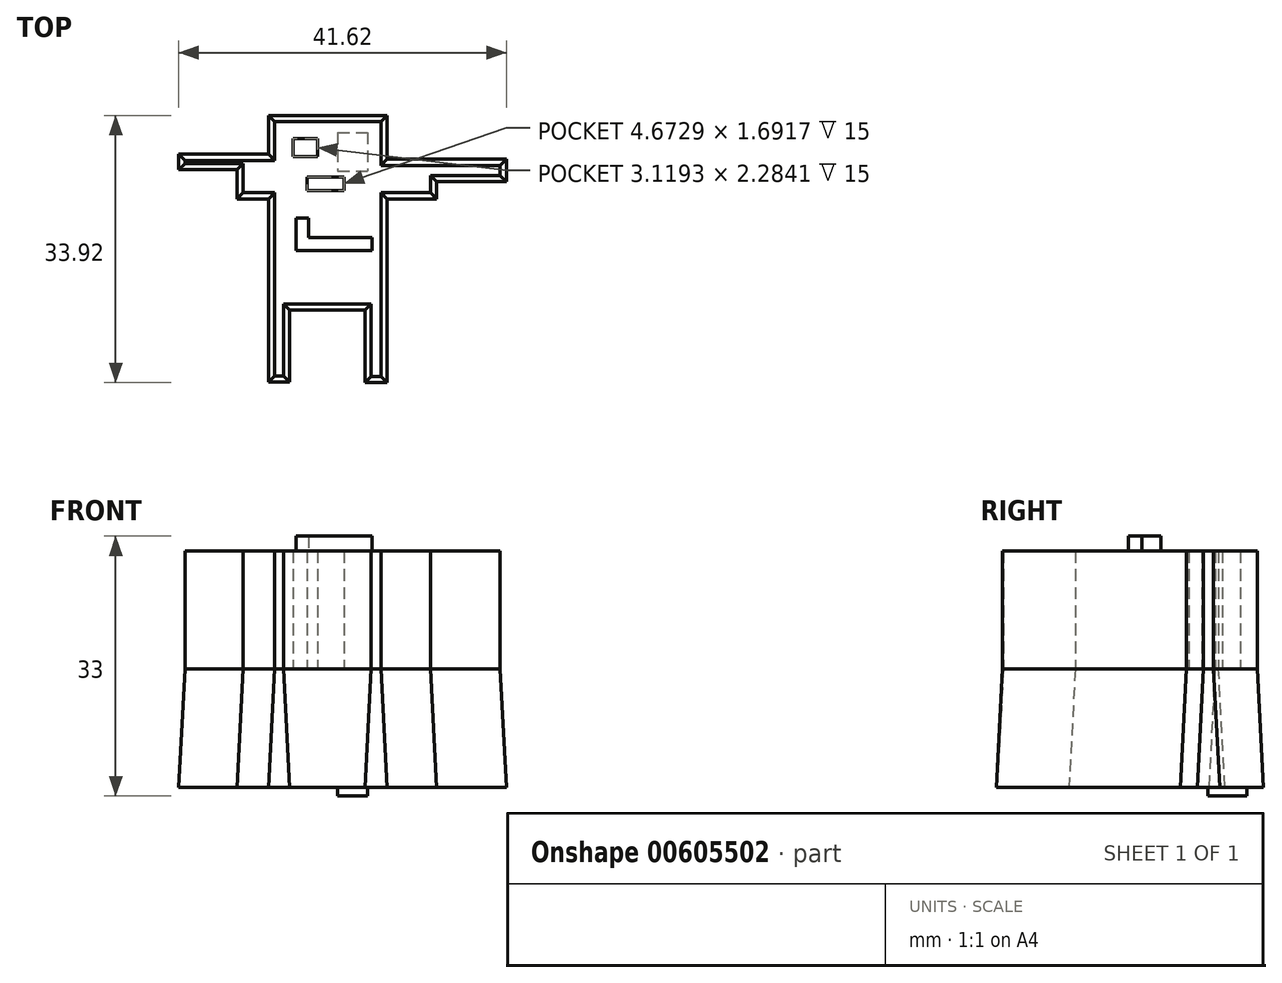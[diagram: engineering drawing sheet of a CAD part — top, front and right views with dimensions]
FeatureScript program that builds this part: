
annotation { "Feature Type Name" : "Feature", "Feature Type Description" : "" }
export const myFeature = defineFeature(function(context is Context, id is Id, definition is map)
    precondition{}
    {
        {
            var Q0;
            Q0=qCreatedBy(makeId("Top.planeOp"),FACE);
            var sketch = newSketch(context, id + "F0", { "sketchPlane" : qUnion([Q0])});
            skLineSegment(sketch, "E0.bottom", {"start": v(-0.5, 23.35) * mm, "end": v(14.55, 23.35) * mm});
            skLineSegment(sketch, "E0.top", {"start": v(-0.5, 9.23) * mm, "end": v(14.55, 9.23) * mm});
            skLineSegment(sketch, "E0.left", {"start": v(-0.5, 23.35) * mm, "end": v(-0.5, 9.23) * mm});
            skLineSegment(sketch, "E0.right", {"start": v(14.55, 23.35) * mm, "end": v(14.55, 9.23) * mm});
            skLineSegment(sketch, "E1.bottom", {"start": v(-0.5, 23.35) * mm, "end": v(-4.53, 23.35) * mm});
            skLineSegment(sketch, "E1.top", {"start": v(-0.5, 29.02) * mm, "end": v(-4.53, 29.02) * mm});
            skLineSegment(sketch, "E1.left", {"start": v(-0.5, 23.35) * mm, "end": v(-0.5, 29.02) * mm});
            skLineSegment(sketch, "E1.right", {"start": v(-4.53, 23.35) * mm, "end": v(-4.53, 29.02) * mm});
            skLineSegment(sketch, "E2.bottom", {"start": v(14.55, 23.35) * mm, "end": v(20.83, 23.35) * mm});
            skLineSegment(sketch, "E2.top", {"start": v(14.55, 28.37) * mm, "end": v(20.83, 28.37) * mm});
            skLineSegment(sketch, "E2.left", {"start": v(14.55, 23.35) * mm, "end": v(14.55, 28.37) * mm});
            skLineSegment(sketch, "E2.right", {"start": v(20.83, 23.35) * mm, "end": v(20.83, 28.37) * mm});
            skLineSegment(sketch, "E3.bottom", {"start": v(14.55, 28.37) * mm, "end": v(-0.5, 28.37) * mm});
            skLineSegment(sketch, "E3.top", {"start": v(14.55, 33.92) * mm, "end": v(-0.5, 33.92) * mm});
            skLineSegment(sketch, "E3.left", {"start": v(14.55, 28.37) * mm, "end": v(14.55, 33.92) * mm});
            skLineSegment(sketch, "E3.right", {"start": v(-0.5, 28.37) * mm, "end": v(-0.5, 33.92) * mm});
            skLineSegment(sketch, "E4.bottom", {"start": v(20.83, 28.37) * mm, "end": v(29.71, 28.37) * mm});
            skLineSegment(sketch, "E4.top", {"start": v(20.83, 25.53) * mm, "end": v(29.71, 25.53) * mm});
            skLineSegment(sketch, "E4.left", {"start": v(20.83, 28.37) * mm, "end": v(20.83, 25.53) * mm});
            skLineSegment(sketch, "E4.right", {"start": v(29.71, 28.37) * mm, "end": v(29.71, 25.53) * mm});
            skLineSegment(sketch, "E5.bottom", {"start": v(-4.53, 29.02) * mm, "end": v(-11.91, 29.02) * mm});
            skLineSegment(sketch, "E5.top", {"start": v(-4.53, 27.04) * mm, "end": v(-11.91, 27.04) * mm});
            skLineSegment(sketch, "E5.left", {"start": v(-4.53, 29.02) * mm, "end": v(-4.53, 27.04) * mm});
            skLineSegment(sketch, "E5.right", {"start": v(-11.91, 29.02) * mm, "end": v(-11.91, 27.04) * mm});
            skLineSegment(sketch, "E6.bottom", {"start": v(-0.5, 9.23) * mm, "end": v(2.2, 9.23) * mm});
            skLineSegment(sketch, "E6.top", {"start": v(-0.5, 0.08) * mm, "end": v(2.2, 0.08) * mm});
            skLineSegment(sketch, "E6.left", {"start": v(-0.5, 9.23) * mm, "end": v(-0.5, 0.08) * mm});
            skLineSegment(sketch, "E6.right", {"start": v(2.2, 9.23) * mm, "end": v(2.2, 0.08) * mm});
            skLineSegment(sketch, "E7.bottom", {"start": v(1.66, 30.36) * mm, "end": v(7.02, 30.36) * mm});
            skLineSegment(sketch, "E7.top", {"start": v(1.66, 28.37) * mm, "end": v(7.02, 28.37) * mm});
            skLineSegment(sketch, "E7.left", {"start": v(1.66, 30.36) * mm, "end": v(1.66, 28.37) * mm});
            skLineSegment(sketch, "E7.right", {"start": v(7.02, 30.36) * mm, "end": v(7.02, 28.37) * mm});
            skLineSegment(sketch, "E8.bottom", {"start": v(27.02, 39.57) * mm, "end": v(-12.98, 39.57) * mm, "construction": true});
            skLineSegment(sketch, "E8.top", {"start": v(27.02, -0.43) * mm, "end": v(-12.98, -0.43) * mm, "construction": true});
            skLineSegment(sketch, "E8.left", {"start": v(27.02, 39.57) * mm, "end": v(27.02, -0.43) * mm, "construction": true});
            skLineSegment(sketch, "E8.right", {"start": v(-12.98, 39.57) * mm, "end": v(-12.98, -0.43) * mm, "construction": true});
            skPoint(sketch, "E8.middle", {"position": v(7.02, 19.57) * mm});
            skPoint(sketch, "E8.middle.positionSnap0", {"position": v(7.02, 29.36) * mm});
            skPoint(sketch, "E8.centerSnap0", {"position": v(7.02, 29.36) * mm});
            skLineSegment(sketch, "E9.bottom", {"start": v(14.55, 9.23) * mm, "end": v(11.73, 9.23) * mm});
            skLineSegment(sketch, "E9.top", {"start": v(14.55, 0) * mm, "end": v(11.73, 0) * mm});
            skLineSegment(sketch, "E9.left", {"start": v(14.55, 9.23) * mm, "end": v(14.55, 0) * mm});
            skLineSegment(sketch, "E9.right", {"start": v(11.73, 9.23) * mm, "end": v(11.73, 0) * mm});
            skSolve(sketch);
        }
        {
            var Q0;
            Q0=makeQuery(id+"F0.imprint","IMPRINT",FACE,{"disambiguationData":[TD([[makeQuery(id+"F0.imprint","IMPRINT",EDGE,{"derivedFrom":sQuery(id+"F0.wireOp",EDGE,"E0.bottom")}),-1.0]])]});
            var Q1;
            {var subQ3=sQuery(id+"F0.wireOp",EDGE,"E2.bottom");Q1=makeQuery(id+"F0.imprint","IMPRINT",FACE,{"disambiguationData":[TD([[makeQuery(id+"F0.imprint","IMPRINT",EDGE,{"derivedFrom":subQ3}),1.0]])]});}
            var Q2;
            {var subQ4=sQuery(id+"F0.wireOp",EDGE,"E0.bottom");Q2=makeQuery(id+"F0.imprint","IMPRINT",FACE,{"disambiguationData":[TD([[makeQuery(id+"F0.imprint","IMPRINT",EDGE,{"derivedFrom":subQ4}),1.0]])]});}
            var Q3;
            {var subQ0=sQuery(id+"F0.wireOp",EDGE,"E5.bottom");Q3=makeQuery(id+"F0.imprint","IMPRINT",FACE,{"disambiguationData":[TD([[makeQuery(id+"F0.imprint","IMPRINT",EDGE,{"derivedFrom":subQ0}),1.0]])]});}
            var Q4;
            {var subQ3=sQuery(id+"F0.wireOp",EDGE,"E1.bottom");Q4=makeQuery(id+"F0.imprint","IMPRINT",FACE,{"disambiguationData":[TD([[makeQuery(id+"F0.imprint","IMPRINT",EDGE,{"derivedFrom":subQ3}),-1.0]])]});}
            var Q5;
            Q5=makeQuery(id+"F0.imprint","IMPRINT",FACE,{"disambiguationData":[TD([[makeQuery(id+"F0.imprint","IMPRINT",EDGE,{"derivedFrom":sQuery(id+"F0.wireOp",EDGE,"E7.bottom")}),-1.0]])]});
            var Q6;
            Q6=makeQuery(id+"F0.imprint","IMPRINT",FACE,{"disambiguationData":[TD([[makeQuery(id+"F0.imprint","IMPRINT",EDGE,{"derivedFrom":sQuery(id+"F0.wireOp",EDGE,"E3.top")}),1.0]])]});
            var Q7;
            Q7=makeQuery(id+"F0.imprint","IMPRINT",FACE,{"disambiguationData":[TD([[makeQuery(id+"F0.imprint","IMPRINT",EDGE,{"derivedFrom":sQuery(id+"F0.wireOp",EDGE,"r1xIN93y-4Mna-sWwQ-LPJp-I6mFRcgzbT0e.bottom")}),1.0]])]});
            var Q8;
            Q8=makeQuery(id+"F0.imprint","IMPRINT",FACE,{"disambiguationData":[TD([[makeQuery(id+"F0.imprint","IMPRINT",EDGE,{"derivedFrom":sQuery(id+"F0.wireOp",EDGE,"E6.top")}),1.0]])]});
            var Q9;
            {var subQ0=sQuery(id+"F0.wireOp",EDGE,"E4.bottom");Q9=makeQuery(id+"F0.imprint","IMPRINT",FACE,{"disambiguationData":[TD([[makeQuery(id+"F0.imprint","IMPRINT",EDGE,{"derivedFrom":subQ0}),-1.0]])]});}
            var Q10;
            Q10=makeQuery(id+"F0.imprint","IMPRINT",FACE,{"disambiguationData":[TD([[makeQuery(id+"F0.imprint","IMPRINT",EDGE,{"derivedFrom":sQuery(id+"F0.wireOp",EDGE,"E9.top")}),-1.0]])]});
            extrude(context, id + "F1", {"entities" : qUnion([Q0, Q1, Q2, Q3, Q4, Q5, Q6, Q7, Q8, Q9, Q10]), "depth" : 15 * mm, "offsetDistance" : 25 * mm, "hasDraft" : true, "draftAngle" : 3 * degree, "draftPullDirection" : true});
        }
        {
            var Q0;
            Q0=makeQuery(id+"F1.opExtrude","CAP_FACE",FACE,{"disambiguationData":[OSD([sQuery(id+"F0.wireOp",EDGE,"E0.top"),sQuery(id+"F0.wireOp",EDGE,"E0.left"),sQuery(id+"F0.wireOp",EDGE,"E0.right"),sQuery(id+"F0.wireOp",EDGE,"E1.bottom"),sQuery(id+"F0.wireOp",EDGE,"E1.top"),sQuery(id+"F0.wireOp",EDGE,"E1.right"),sQuery(id+"F0.wireOp",EDGE,"E2.bottom"),sQuery(id+"F0.wireOp",EDGE,"E2.top"),sQuery(id+"F0.wireOp",EDGE,"E2.right"),sQuery(id+"F0.wireOp",EDGE,"E3.top"),sQuery(id+"F0.wireOp",EDGE,"E3.left"),sQuery(id+"F0.wireOp",EDGE,"E3.right"),sQuery(id+"F0.wireOp",EDGE,"E4.bottom"),sQuery(id+"F0.wireOp",EDGE,"E4.top"),sQuery(id+"F0.wireOp",EDGE,"E4.right"),sQuery(id+"F0.wireOp",EDGE,"E5.bottom"),sQuery(id+"F0.wireOp",EDGE,"E5.top"),sQuery(id+"F0.wireOp",EDGE,"E5.right"),sQuery(id+"F0.wireOp",EDGE,"E6.top"),sQuery(id+"F0.wireOp",EDGE,"E6.left"),sQuery(id+"F0.wireOp",EDGE,"E6.right"),sQuery(id+"F0.wireOp",EDGE,"E9.top"),sQuery(id+"F0.wireOp",EDGE,"E9.left"),sQuery(id+"F0.wireOp",EDGE,"E9.right")])],"isStart":false});
            var sketch = newSketch(context, id + "F2", { "sketchPlane" : qUnion([Q0])});
            skLineSegment(sketch, "E10.bottom", {"start": v(2.6, 31) * mm, "end": v(5.71, 31) * mm});
            skLineSegment(sketch, "E10.top", {"start": v(2.6, 28.72) * mm, "end": v(5.71, 28.72) * mm});
            skLineSegment(sketch, "E10.left", {"start": v(2.6, 31) * mm, "end": v(2.6, 28.72) * mm});
            skLineSegment(sketch, "E10.right", {"start": v(5.71, 31) * mm, "end": v(5.71, 28.72) * mm});
            skLineSegment(sketch, "E11.bottom", {"start": v(4.4, 26.11) * mm, "end": v(9.08, 26.11) * mm});
            skLineSegment(sketch, "E11.top", {"start": v(4.4, 24.42) * mm, "end": v(9.08, 24.42) * mm});
            skLineSegment(sketch, "E11.left", {"start": v(4.4, 26.11) * mm, "end": v(4.4, 24.42) * mm});
            skLineSegment(sketch, "E11.right", {"start": v(9.08, 26.11) * mm, "end": v(9.08, 24.42) * mm});
            skSolve(sketch);
        }
        {
            var Q0;
            Q0=makeQuery(id+"F2.imprint","IMPRINT",FACE,{"disambiguationData":[TD([[makeQuery(id+"F2.imprint","IMPRINT",EDGE,{"derivedFrom":sQuery(id+"F2.wireOp",EDGE,"E10.bottom")}),1.0]])]});
            var sketch = newSketch(context, id + "F3", { "sketchPlane" : qUnion([Q0])});
            skLineSegment(sketch, "E12.bottom", {"start": v(8.23, 31.04) * mm, "end": v(11.91, 31.04) * mm});
            skLineSegment(sketch, "E12.top", {"start": v(8.23, 27.89) * mm, "end": v(11.91, 27.89) * mm});
            skLineSegment(sketch, "E12.left", {"start": v(8.23, 31.04) * mm, "end": v(8.23, 27.89) * mm});
            skLineSegment(sketch, "E12.right", {"start": v(11.91, 31.04) * mm, "end": v(11.91, 27.89) * mm});
            skSolve(sketch);
        }
        {
            var Q0;
            Q0=makeQuery(id+"F2.imprint","IMPRINT",FACE,{"disambiguationData":[TD([[makeQuery(id+"F2.imprint","IMPRINT",EDGE,{"derivedFrom":sQuery(id+"F2.wireOp",EDGE,"E10.bottom")}),1.0]])]});
            var Q1;
            Q1=makeQuery(id+"F3.imprint","IMPRINT",FACE,{"disambiguationData":[TD([[makeQuery(id+"F3.imprint","IMPRINT",EDGE,{"derivedFrom":sQuery(id+"F3.wireOp",EDGE,"E12.bottom")}),-1.0]])]});
            extrude(context, id + "F4", {"entities" : qUnion([Q0, Q1]), "operationType" : NewBodyOperationType.ADD, "depth" : 15 * mm, "offsetDistance" : 25 * mm});
        }
        {
            var Q0;
            Q0=makeQuery(id+"F4.opExtrude","CAP_FACE",FACE,{"disambiguationData":[OSD([sQuery(id+"F0.wireOp",EDGE,"E0.top"),sQuery(id+"F0.wireOp",EDGE,"E0.left"),sQuery(id+"F0.wireOp",EDGE,"E0.right"),sQuery(id+"F0.wireOp",EDGE,"E1.bottom"),sQuery(id+"F0.wireOp",EDGE,"E1.top"),sQuery(id+"F0.wireOp",EDGE,"E1.right"),sQuery(id+"F0.wireOp",EDGE,"E2.bottom"),sQuery(id+"F0.wireOp",EDGE,"E2.top"),sQuery(id+"F0.wireOp",EDGE,"E2.right"),sQuery(id+"F0.wireOp",EDGE,"E3.top"),sQuery(id+"F0.wireOp",EDGE,"E3.left"),sQuery(id+"F0.wireOp",EDGE,"E3.right"),sQuery(id+"F0.wireOp",EDGE,"E4.bottom"),sQuery(id+"F0.wireOp",EDGE,"E4.top"),sQuery(id+"F0.wireOp",EDGE,"E4.right"),sQuery(id+"F0.wireOp",EDGE,"E5.bottom"),sQuery(id+"F0.wireOp",EDGE,"E5.top"),sQuery(id+"F0.wireOp",EDGE,"E5.right"),sQuery(id+"F0.wireOp",EDGE,"E6.top"),sQuery(id+"F0.wireOp",EDGE,"E6.left"),sQuery(id+"F0.wireOp",EDGE,"E6.right"),sQuery(id+"F0.wireOp",EDGE,"E9.top"),sQuery(id+"F0.wireOp",EDGE,"E9.left"),sQuery(id+"F0.wireOp",EDGE,"E9.right"),sQuery(id+"F2.wireOp",EDGE,"E10.bottom"),sQuery(id+"F2.wireOp",EDGE,"E10.top"),sQuery(id+"F2.wireOp",EDGE,"E10.left"),sQuery(id+"F2.wireOp",EDGE,"E10.right"),sQuery(id+"F2.wireOp",EDGE,"E11.bottom"),sQuery(id+"F2.wireOp",EDGE,"E11.top"),sQuery(id+"F2.wireOp",EDGE,"E11.left"),sQuery(id+"F2.wireOp",EDGE,"E11.right")])],"isStart":false});
            var sketch = newSketch(context, id + "F5", { "sketchPlane" : qUnion([Q0])});
            skLineSegment(sketch, "E13.bottom", {"start": v(8.28, 31.8) * mm, "end": v(12.06, 31.8) * mm});
            skLineSegment(sketch, "E13.top", {"start": v(8.28, 26.87) * mm, "end": v(12.06, 26.87) * mm});
            skLineSegment(sketch, "E13.left", {"start": v(8.28, 31.8) * mm, "end": v(8.28, 26.87) * mm});
            skLineSegment(sketch, "E13.right", {"start": v(12.06, 31.8) * mm, "end": v(12.06, 26.87) * mm});
            skPoint(sketch, "E14.oppositeSnap0", {"position": v(8.28, 29.33) * mm});
            skLineSegment(sketch, "E14.bottom", {"start": v(8.28, 29.33) * mm, "end": v(6.8, 29.33) * mm});
            skLineSegment(sketch, "E14.top", {"start": v(8.28, 29.33) * mm, "end": v(6.8, 29.33) * mm});
            skLineSegment(sketch, "E14.left", {"start": v(8.28, 29.33) * mm, "end": v(8.28, 29.33) * mm});
            skLineSegment(sketch, "E14.right", {"start": v(6.8, 29.33) * mm, "end": v(6.8, 29.33) * mm});
            skSolve(sketch);
        }
        {
            var Q0;
            {var subQ3=sQuery(id+"F5.wireOp",EDGE,"E13.bottom");Q0=makeQuery(id+"F5.imprint","IMPRINT",FACE,{"disambiguationData":[TD([[makeQuery(id+"F5.imprint","IMPRINT",EDGE,{"derivedFrom":subQ3}),-1.0]])]});}
            extrude(context, id + "F6", {"entities" : qUnion([Q0]), "operationType" : NewBodyOperationType.ADD, "oppositeDirection" : true, "depth" : 31.1 * mm, "offsetDistance" : 25 * mm});
        }
        {
            var Q0;
            Q0=makeQuery(id+"F4.opExtrude","CAP_FACE",FACE,{"disambiguationData":[OSD([sQuery(id+"F0.wireOp",EDGE,"E0.top"),sQuery(id+"F0.wireOp",EDGE,"E0.left"),sQuery(id+"F0.wireOp",EDGE,"E0.right"),sQuery(id+"F0.wireOp",EDGE,"E1.bottom"),sQuery(id+"F0.wireOp",EDGE,"E1.top"),sQuery(id+"F0.wireOp",EDGE,"E1.right"),sQuery(id+"F0.wireOp",EDGE,"E2.bottom"),sQuery(id+"F0.wireOp",EDGE,"E2.top"),sQuery(id+"F0.wireOp",EDGE,"E2.right"),sQuery(id+"F0.wireOp",EDGE,"E3.top"),sQuery(id+"F0.wireOp",EDGE,"E3.left"),sQuery(id+"F0.wireOp",EDGE,"E3.right"),sQuery(id+"F0.wireOp",EDGE,"E4.bottom"),sQuery(id+"F0.wireOp",EDGE,"E4.top"),sQuery(id+"F0.wireOp",EDGE,"E4.right"),sQuery(id+"F0.wireOp",EDGE,"E5.bottom"),sQuery(id+"F0.wireOp",EDGE,"E5.top"),sQuery(id+"F0.wireOp",EDGE,"E5.right"),sQuery(id+"F0.wireOp",EDGE,"E6.top"),sQuery(id+"F0.wireOp",EDGE,"E6.left"),sQuery(id+"F0.wireOp",EDGE,"E6.right"),sQuery(id+"F0.wireOp",EDGE,"E9.top"),sQuery(id+"F0.wireOp",EDGE,"E9.left"),sQuery(id+"F0.wireOp",EDGE,"E9.right"),sQuery(id+"F2.wireOp",EDGE,"E10.bottom"),sQuery(id+"F2.wireOp",EDGE,"E10.top"),sQuery(id+"F2.wireOp",EDGE,"E10.left"),sQuery(id+"F2.wireOp",EDGE,"E10.right"),sQuery(id+"F2.wireOp",EDGE,"E11.bottom"),sQuery(id+"F2.wireOp",EDGE,"E11.top"),sQuery(id+"F2.wireOp",EDGE,"E11.left"),sQuery(id+"F2.wireOp",EDGE,"E11.right")])],"isStart":false});
            var sketch = newSketch(context, id + "F7", { "sketchPlane" : qUnion([Q0])});
            skLineSegment(sketch, "E15.bottom", {"start": v(2.97, 20.9) * mm, "end": v(4.55, 20.9) * mm});
            skLineSegment(sketch, "E15.top", {"start": v(2.97, 16.76) * mm, "end": v(4.01, 16.76) * mm});
            skLineSegment(sketch, "E15.left", {"start": v(2.97, 20.9) * mm, "end": v(2.97, 16.76) * mm});
            skLineSegment(sketch, "E16.bottom", {"start": v(4.01, 16.76) * mm, "end": v(8.46, 16.76) * mm});
            skLineSegment(sketch, "E16.top", {"start": v(4.55, 18.46) * mm, "end": v(8.46, 18.46) * mm});
            skLineSegment(sketch, "E17.bottom", {"start": v(8.46, 18.46) * mm, "end": v(12.63, 18.46) * mm});
            skLineSegment(sketch, "E17.top", {"start": v(8.46, 16.76) * mm, "end": v(12.63, 16.76) * mm});
            skLineSegment(sketch, "E17.right", {"start": v(12.63, 18.46) * mm, "end": v(12.63, 16.76) * mm});
            skLineSegment(sketch, "E18.bottom", {"start": v(12.63, 18.46) * mm, "end": v(11.39, 18.46) * mm});
            skLineSegment(sketch, "E18.top", {"start": v(12.63, 20.9) * mm, "end": v(11.39, 20.9) * mm});
            skLineSegment(sketch, "E18.left", {"start": v(12.63, 18.46) * mm, "end": v(12.63, 20.9) * mm});
            skLineSegment(sketch, "E18.right", {"start": v(11.39, 18.46) * mm, "end": v(11.39, 20.9) * mm});
            skLineSegment(sketch, "E19", {"start": v(4.55, 20.9) * mm, "end": v(4.55, 18.46) * mm});
            skSolve(sketch);
        }
        {
            var Q0;
            Q0=makeQuery(id+"F7.imprint","IMPRINT",FACE,{"disambiguationData":[TD([[makeQuery(id+"F7.imprint","IMPRINT",EDGE,{"derivedFrom":sQuery(id+"F7.wireOp",EDGE,"E15.bottom")}),-1.0]])]});
            var Q1;
            Q1=makeQuery(id+"F7.imprint","IMPRINT",FACE,{"disambiguationData":[TD([[makeQuery(id+"F7.imprint","IMPRINT",EDGE,{"derivedFrom":sQuery(id+"F7.wireOp",EDGE,"E18.bottom")}),-1.0]])]});
            extrude(context, id + "F8", {"entities" : qUnion([Q0, Q1]), "operationType" : NewBodyOperationType.ADD, "depth" : 1.9 * mm, "offsetDistance" : 25 * mm});
        }
        {
            var Q0;
            Q0=makeQuery(id+"F4.opExtrude","CAP_FACE",FACE,{"disambiguationData":[OSD([sQuery(id+"F0.wireOp",EDGE,"E0.top"),sQuery(id+"F0.wireOp",EDGE,"E0.left"),sQuery(id+"F0.wireOp",EDGE,"E0.right"),sQuery(id+"F0.wireOp",EDGE,"E1.bottom"),sQuery(id+"F0.wireOp",EDGE,"E1.top"),sQuery(id+"F0.wireOp",EDGE,"E1.right"),sQuery(id+"F0.wireOp",EDGE,"E2.bottom"),sQuery(id+"F0.wireOp",EDGE,"E2.top"),sQuery(id+"F0.wireOp",EDGE,"E2.right"),sQuery(id+"F0.wireOp",EDGE,"E3.top"),sQuery(id+"F0.wireOp",EDGE,"E3.left"),sQuery(id+"F0.wireOp",EDGE,"E3.right"),sQuery(id+"F0.wireOp",EDGE,"E4.bottom"),sQuery(id+"F0.wireOp",EDGE,"E4.top"),sQuery(id+"F0.wireOp",EDGE,"E4.right"),sQuery(id+"F0.wireOp",EDGE,"E5.bottom"),sQuery(id+"F0.wireOp",EDGE,"E5.top"),sQuery(id+"F0.wireOp",EDGE,"E5.right"),sQuery(id+"F0.wireOp",EDGE,"E6.top"),sQuery(id+"F0.wireOp",EDGE,"E6.left"),sQuery(id+"F0.wireOp",EDGE,"E6.right"),sQuery(id+"F0.wireOp",EDGE,"E9.top"),sQuery(id+"F0.wireOp",EDGE,"E9.left"),sQuery(id+"F0.wireOp",EDGE,"E9.right"),sQuery(id+"F2.wireOp",EDGE,"E10.bottom"),sQuery(id+"F2.wireOp",EDGE,"E10.top"),sQuery(id+"F2.wireOp",EDGE,"E10.left"),sQuery(id+"F2.wireOp",EDGE,"E10.right"),sQuery(id+"F2.wireOp",EDGE,"E11.bottom"),sQuery(id+"F2.wireOp",EDGE,"E11.top"),sQuery(id+"F2.wireOp",EDGE,"E11.left"),sQuery(id+"F2.wireOp",EDGE,"E11.right")])],"isStart":false});
            var sketch = newSketch(context, id + "F9", { "sketchPlane" : qUnion([Q0])});
            skLineSegment(sketch, "E20.bottom", {"start": v(9.2, 31) * mm, "end": v(11.95, 31) * mm});
            skLineSegment(sketch, "E20.top", {"start": v(9.2, 29.1) * mm, "end": v(11.95, 29.1) * mm});
            skLineSegment(sketch, "E20.left", {"start": v(9.2, 31) * mm, "end": v(9.2, 29.1) * mm});
            skLineSegment(sketch, "E20.right", {"start": v(11.95, 31) * mm, "end": v(11.95, 29.1) * mm});
            skSolve(sketch);
        }
        {
            var Q0;
            Q0 = qSketchRegion(id + "F9", true);
            extrude(context, id + "F10", {"entities" : qUnion([Q0]), "operationType" : NewBodyOperationType.ADD, "oppositeDirection" : true, "depth" : 29.8 * mm, "offsetDistance" : 25 * mm});
        }
        {
            var Q0;
            Q0=qCreatedBy(makeId("Top.planeOp"),FACE);
            var sketch = newSketch(context, id + "F11", { "sketchPlane" : qUnion([Q0])});
            skLineSegment(sketch, "E21", {"start": v(8.26, 30.62) * mm, "end": v(8.26, 28.72) * mm});
            skLineSegment(sketch, "E22", {"start": v(8.26, 28.72) * mm, "end": v(10.74, 28.72) * mm});
            skLineSegment(sketch, "E23", {"start": v(10.74, 28.72) * mm, "end": v(10.74, 30.62) * mm});
            skLineSegment(sketch, "E24", {"start": v(10.74, 30.62) * mm, "end": v(8.26, 30.62) * mm});
            skLineSegment(sketch, "E25", {"start": v(9.5, 30.62) * mm, "end": v(9.5, 28.72) * mm});
            skLineSegment(sketch, "E26", {"start": v(9.5, 28.72) * mm, "end": v(8.96, 30.62) * mm});
            skLineSegment(sketch, "E27", {"start": v(8.96, 30.62) * mm, "end": v(8.96, 28.72) * mm});
            skLineSegment(sketch, "E28", {"start": v(3.77, 30.97) * mm, "end": v(3.77, 28.78) * mm});
            skLineSegment(sketch, "E29", {"start": v(3.77, 28.78) * mm, "end": v(4.4, 31.14) * mm});
            skLineSegment(sketch, "E30", {"start": v(4.4, 31.14) * mm, "end": v(4.4, 28.72) * mm});
            skSolve(sketch);
        }
        {
            var Q0;
            {var subQ0=sQuery(id+"F11.wireOp",EDGE,"E21");Q0=makeQuery(id+"F11.imprint","IMPRINT",FACE,{"disambiguationData":[TD([[makeQuery(id+"F11.imprint","IMPRINT",EDGE,{"derivedFrom":subQ0}),1.0]])]});}
            var Q1;
            {var subQ0=sQuery(id+"F11.wireOp",EDGE,"E23");Q1=makeQuery(id+"F11.imprint","IMPRINT",FACE,{"disambiguationData":[TD([[makeQuery(id+"F11.imprint","IMPRINT",EDGE,{"derivedFrom":subQ0}),1.0]])]});}
            var Q2;
            {var subQ0=sQuery(id+"F11.wireOp",EDGE,"E26");Q2=makeQuery(id+"F11.imprint","IMPRINT",FACE,{"disambiguationData":[TD([[makeQuery(id+"F11.imprint","IMPRINT",EDGE,{"derivedFrom":subQ0}),1.0]])]});}
            var Q3;
            {var subQ0=sQuery(id+"F11.wireOp",EDGE,"E25");Q3=makeQuery(id+"F11.imprint","IMPRINT",FACE,{"disambiguationData":[TD([[makeQuery(id+"F11.imprint","IMPRINT",EDGE,{"derivedFrom":subQ0}),-1.0]])]});}
            extrude(context, id + "F12", {"entities" : qUnion([Q0, Q1, Q2, Q3]), "operationType" : NewBodyOperationType.ADD, "depth" : 28.9 * mm, "offsetDistance" : 25 * mm});
        }
    });
